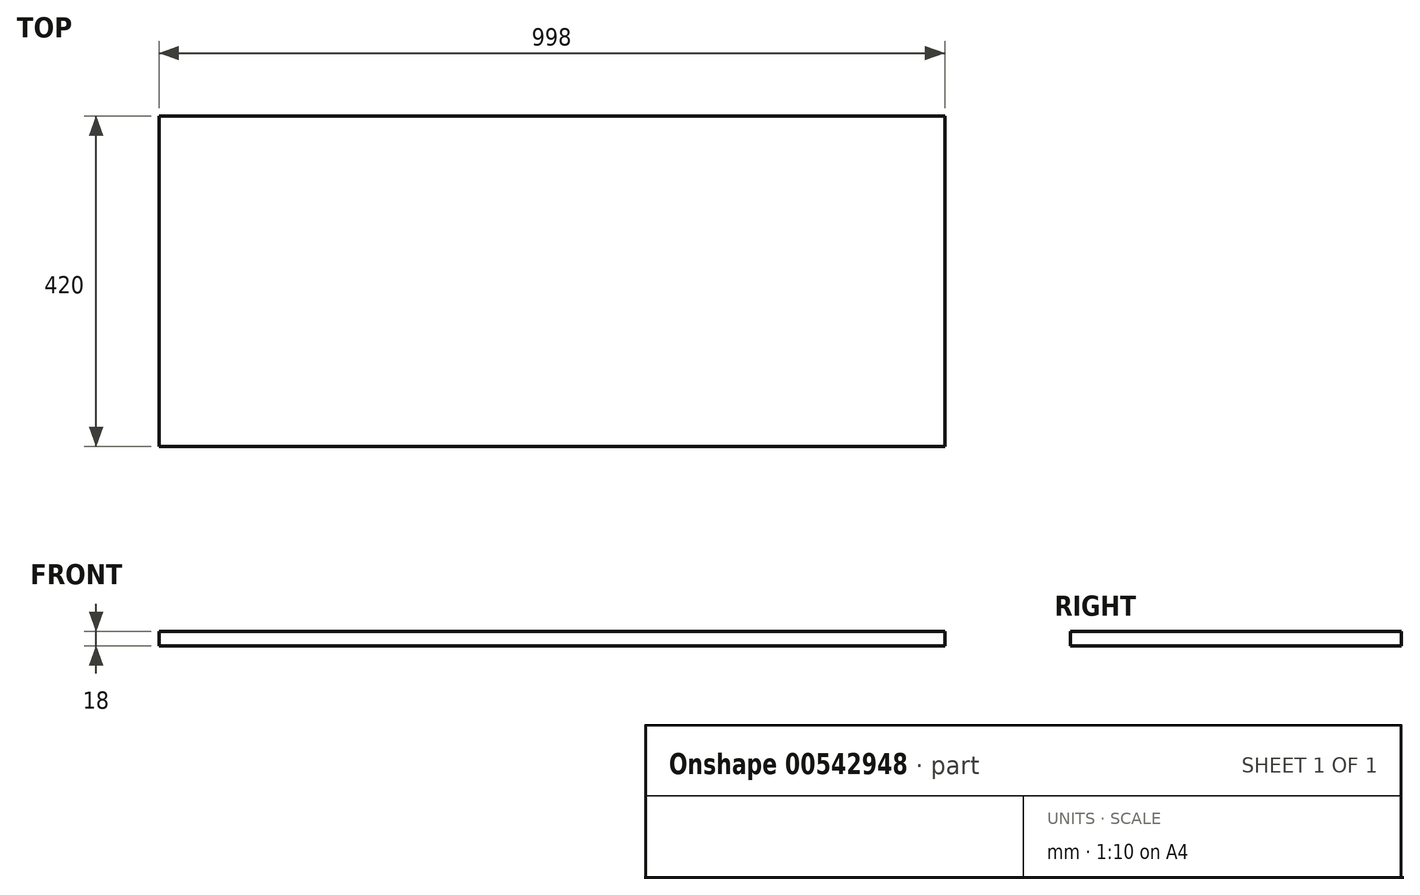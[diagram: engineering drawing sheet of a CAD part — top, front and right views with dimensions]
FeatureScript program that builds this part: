
annotation { "Feature Type Name" : "Feature", "Feature Type Description" : "" }
export const myFeature = defineFeature(function(context is Context, id is Id, definition is map)
    precondition{}
    {
        {
            var Q0;
            Q0=qCreatedBy(makeId("Front.planeOp"),FACE);
            var sketch = newSketch(context, id + "F0", { "sketchPlane" : qUnion([Q0])});
            skLineSegment(sketch, "E0.bottom", {"start": v(-47.45, -41.16) * mm, "end": v(950.55, -41.16) * mm});
            skLineSegment(sketch, "E0.top", {"start": v(-47.45, -23.16) * mm, "end": v(950.55, -23.16) * mm});
            skLineSegment(sketch, "E0.left", {"start": v(-47.45, -41.16) * mm, "end": v(-47.45, -23.16) * mm});
            skLineSegment(sketch, "E0.right", {"start": v(950.55, -41.16) * mm, "end": v(950.55, -23.16) * mm});
            skSolve(sketch);
        }
        {
            var Q0;
            Q0 = qSketchRegion(id + "F0", true);
            extrude(context, id + "F1", {"entities" : qUnion([Q0]), "oppositeDirection" : true, "depth" : 420 * mm, "offsetDistance" : 25 * mm});
        }
    });
